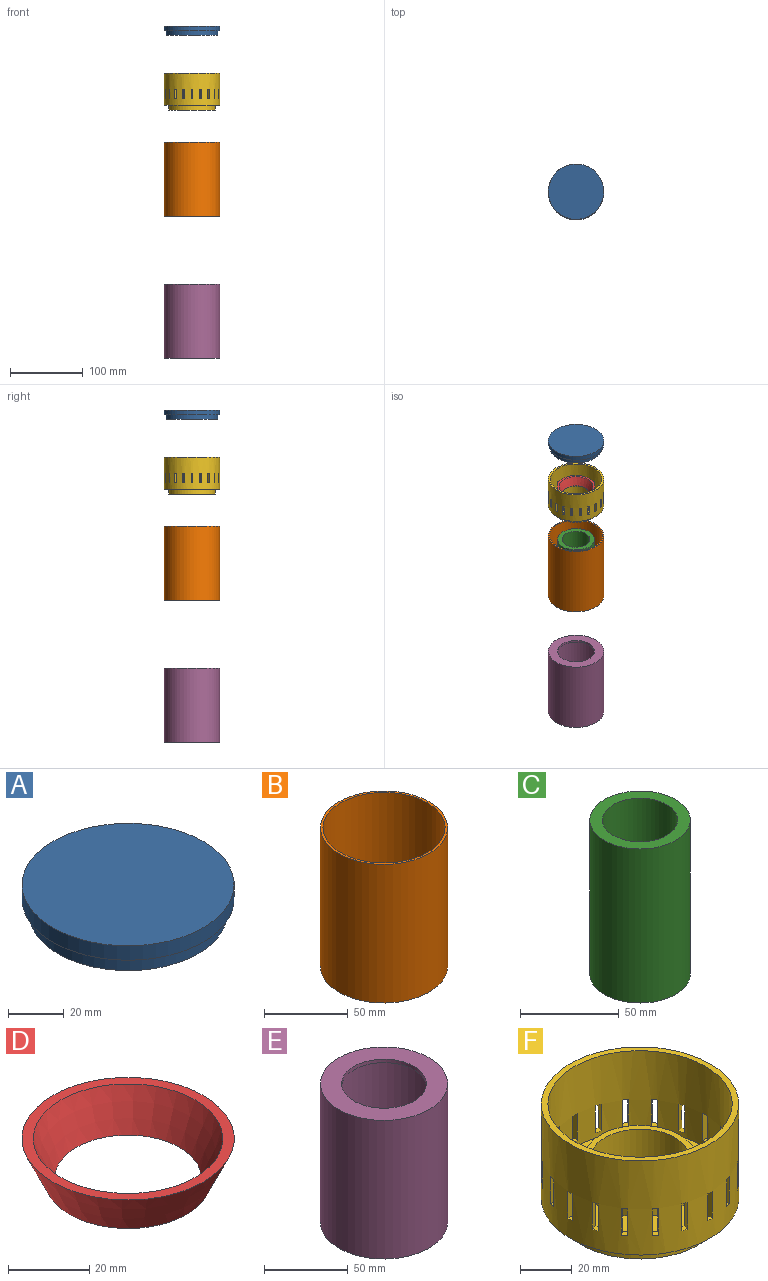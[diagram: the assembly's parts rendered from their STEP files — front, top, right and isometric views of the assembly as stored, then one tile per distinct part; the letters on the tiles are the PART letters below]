
ASSEMBLY  parts=6 mates=2
PART A: 5 faces, bbox 76.2x76.2x12.7 mm
  f0: cylinder r=38.1mm len=76.2mm, axis (0,0,-1), area 1520.1mm2, adj f1,f2
  f1: plane 76.2x76.2mm, normal (0,0,1), area 4560.4mm2, adj f0
  f2: plane 76.2x76.2mm, normal (0,0,-1), area 587.8mm2, adj f0,f3
  f3: cylinder r=35.56mm len=71.12mm, axis (0,0,1), area 1418.8mm2, adj f2,f4
  f4: plane 71.12x71.12mm, normal (0,0,-1), area 3972.6mm2, adj f3
PART B: 4 faces, bbox 76.2x76.2x101.6 mm
  f0: cylinder r=36.58mm len=101.6mm, axis (0,0,-1), area 23349.1mm2, adj f2,f3
  f1: cylinder r=38.1mm len=101.6mm, axis (0,0,-1), area 24322mm2, adj f2,f3
  f2: plane 76.2x76.2mm, normal (0,0,1), area 357.5mm2, adj f0,f1
  f3: plane 76.2x76.2mm, normal (0,0,-1), area 357.5mm2, adj f0,f1
PART C: 4 faces, bbox 50.8x50.8x95.3 mm
  f0: cylinder r=19.05mm len=95.25mm, axis (0,0,-1), area 11400.9mm2, adj f2,f3
  f1: cylinder r=25.4mm len=95.25mm, axis (0,0,-1), area 15201.2mm2, adj f2,f3
  f2: plane 50.8x50.8mm, normal (0,0,1), area 886.7mm2, adj f0,f1
  f3: plane 50.8x50.8mm, normal (0,0,-1), area 886.7mm2, adj f0,f1
PART D: 4 faces, bbox 52.3x52.3x12.7 mm
  f0: cone r=20.32mm half-angle=65.4deg, axis (0,0,-1), area 305.9mm2, adj f1,f2
  f1: cone r=18.01mm half-angle=24.6deg, axis (0,0,1), area 1663.8mm2, adj f0,f3
  f2: cone r=20.32mm half-angle=24.6deg, axis (0,0,1), area 2039mm2, adj f0,f3
  f3: plane 52.28x52.28mm, normal (0,0,1), area 434.4mm2, adj f1,f2
PART E: 6 faces, bbox 76.2x76.2x101.6 mm
  f0: cylinder r=35.56mm len=99.06mm, axis (0,0,-1), area 22133mm2, adj f4,f5
  f1: cylinder r=38.1mm len=101.6mm, axis (0,0,-1), area 24322mm2, adj f2,f5
  f2: plane 76.2x76.2mm, normal (0,0,1), area 2533.5mm2, adj f1,f3
  f3: cylinder r=25.4mm len=50.8mm, axis (0,0,1), area 405.4mm2, adj f2,f4
  f4: plane 71.12x71.12mm, normal (0,0,-1), area 1945.8mm2, adj f0,f3
  f5: plane 76.2x76.2mm, normal (0,0,-1), area 587.8mm2, adj f0,f1
PART F: 90 faces, bbox 76.2x76.2x50.8 mm
  f0: cylinder r=19.05mm len=38.1mm, axis (0,0,-1), area 3040.2mm2, adj f2,f7
  f1: cylinder r=21.59mm len=43.18mm, axis (0,0,-1), area 1722.8mm2, adj f2,f3
  f2: plane 43.18x43.18mm, normal (0,0,1), area 324.3mm2, adj f0,f1
  f3: plane 71.12x71.12mm, normal (0,0,1), area 2508.2mm2, adj f1,f84
  f4: cylinder r=38.1mm len=76.2mm, axis (0,0,1), area 9995.6mm2, adj f5,f8,f9,f10,f11,f12,f13,f14
  f5: plane 76.2x76.2mm, normal (0,0,-1), area 1393.4mm2, adj f4,f6
  f6: cylinder r=31.75mm len=63.5mm, axis (0,0,1), area 1266.8mm2, adj f5,f7
  f7: plane 63.5x63.5mm, normal (0,0,-1), area 2026.8mm2, adj f0,f6
  f8: plane 12.7x2.42mm, normal (0.95,-0.31,0), area 32.3mm2, adj f4,f9,f11,f84
  f9: plane 3.2x3.2mm, normal (0,0,1), area 6.5mm2, adj f4,f8,f10,f84
  f10: plane 12.7x2.42mm, normal (-0.95,0.31,0), area 32.3mm2, adj f4,f9,f11,f84
  f11: plane 3.2x3.2mm, normal (0,0,-1), area 6.5mm2, adj f4,f8,f10,f84
  f12: plane 12.7x2.06mm, normal (0.81,-0.59,0), area 32.3mm2, adj f4,f13,f15,f84
  f13: plane 3.55x3.55mm, normal (0,0,1), area 6.5mm2, adj f4,f12,f14,f84
  f14: plane 12.7x2.06mm, normal (-0.81,0.59,0), area 32.3mm2, adj f4,f13,f15,f84
  f15: plane 3.55x3.55mm, normal (0,0,-1), area 6.5mm2, adj f4,f12,f14,f84
  f16: plane 12.7x2.06mm, normal (0.59,-0.81,0), area 32.3mm2, adj f4,f17,f19,f84
  f17: plane 3.55x3.55mm, normal (0,0,1), area 6.5mm2, adj f4,f16,f18,f84
  f18: plane 12.7x2.06mm, normal (-0.59,0.81,0), area 32.3mm2, adj f4,f17,f19,f84
  f19: plane 3.55x3.55mm, normal (0,0,-1), area 6.5mm2, adj f4,f16,f18,f84
  f20: plane 12.7x2.42mm, normal (0.31,-0.95,0), area 32.3mm2, adj f4,f21,f23,f84
  f21: plane 3.2x3.2mm, normal (0,0,1), area 6.5mm2, adj f4,f20,f22,f84
  f22: plane 12.7x2.42mm, normal (-0.31,0.95,0), area 32.3mm2, adj f4,f21,f23,f84
  f23: plane 3.2x3.2mm, normal (0,0,-1), area 6.5mm2, adj f4,f20,f22,f84
  f24: plane 12.7x2.54mm, normal (0,-1,0), area 32.3mm2, adj f4,f25,f27,f84
  f25: plane 2.56x2.54mm, normal (0,0,1), area 6.5mm2, adj f4,f24,f26,f84
  f26: plane 12.7x2.54mm, normal (0,1,0), area 32.3mm2, adj f4,f25,f27,f84
  f27: plane 2.56x2.54mm, normal (0,0,-1), area 6.5mm2, adj f4,f24,f26,f84
  f28: plane 12.7x2.42mm, normal (-0.31,-0.95,0), area 32.3mm2, adj f4,f29,f31,f84
  f29: plane 3.2x3.2mm, normal (0,0,1), area 6.5mm2, adj f4,f28,f30,f84
  f30: plane 12.7x2.42mm, normal (0.31,0.95,0), area 32.3mm2, adj f4,f29,f31,f84
  f31: plane 3.2x3.2mm, normal (0,0,-1), area 6.5mm2, adj f4,f28,f30,f84
  f32: plane 12.7x2.06mm, normal (-0.59,-0.81,0), area 32.3mm2, adj f4,f33,f35,f84
  f33: plane 3.55x3.55mm, normal (0,0,1), area 6.5mm2, adj f4,f32,f34,f84
  f34: plane 12.7x2.06mm, normal (0.59,0.81,0), area 32.3mm2, adj f4,f33,f35,f84
  f35: plane 3.55x3.55mm, normal (0,0,-1), area 6.5mm2, adj f4,f32,f34,f84
  f36: plane 12.7x2.06mm, normal (-0.81,-0.59,0), area 32.3mm2, adj f4,f37,f39,f84
  f37: plane 3.55x3.55mm, normal (0,0,1), area 6.5mm2, adj f4,f36,f38,f84
  f38: plane 12.7x2.06mm, normal (0.81,0.59,0), area 32.3mm2, adj f4,f37,f39,f84
  f39: plane 3.55x3.55mm, normal (0,0,-1), area 6.5mm2, adj f4,f36,f38,f84
  f40: plane 12.7x2.42mm, normal (-0.95,-0.31,0), area 32.3mm2, adj f4,f41,f43,f84
  f41: plane 3.2x3.2mm, normal (0,0,1), area 6.5mm2, adj f4,f40,f42,f84
  f42: plane 12.7x2.42mm, normal (0.95,0.31,0), area 32.3mm2, adj f4,f41,f43,f84
  f43: plane 3.2x3.2mm, normal (0,0,-1), area 6.5mm2, adj f4,f40,f42,f84
  f44: plane 12.7x2.54mm, normal (-1,0,0), area 32.3mm2, adj f4,f45,f47,f84
  f45: plane 2.56x2.54mm, normal (0,0,1), area 6.5mm2, adj f4,f44,f46,f84
  f46: plane 12.7x2.54mm, normal (1,0,0), area 32.3mm2, adj f4,f45,f47,f84
  f47: plane 2.56x2.54mm, normal (0,0,-1), area 6.5mm2, adj f4,f44,f46,f84
  f48: plane 12.7x2.42mm, normal (-0.95,0.31,0), area 32.3mm2, adj f4,f49,f51,f84
  f49: plane 3.2x3.2mm, normal (0,0,1), area 6.5mm2, adj f4,f48,f50,f84
  f50: plane 12.7x2.42mm, normal (0.95,-0.31,0), area 32.3mm2, adj f4,f49,f51,f84
  f51: plane 3.2x3.2mm, normal (0,0,-1), area 6.5mm2, adj f4,f48,f50,f84
  f52: plane 12.7x2.06mm, normal (-0.81,0.59,0), area 32.3mm2, adj f4,f53,f55,f84
  f53: plane 3.55x3.55mm, normal (0,0,1), area 6.5mm2, adj f4,f52,f54,f84
  f54: plane 12.7x2.06mm, normal (0.81,-0.59,0), area 32.3mm2, adj f4,f53,f55,f84
  f55: plane 3.55x3.55mm, normal (0,0,-1), area 6.5mm2, adj f4,f52,f54,f84
  f56: plane 12.7x2.06mm, normal (-0.59,0.81,0), area 32.3mm2, adj f4,f57,f59,f84
  f57: plane 3.55x3.55mm, normal (0,0,1), area 6.5mm2, adj f4,f56,f58,f84
  f58: plane 12.7x2.06mm, normal (0.59,-0.81,0), area 32.3mm2, adj f4,f57,f59,f84
  f59: plane 3.55x3.55mm, normal (0,0,-1), area 6.5mm2, adj f4,f56,f58,f84
  f60: plane 12.7x2.42mm, normal (-0.31,0.95,0), area 32.3mm2, adj f4,f61,f63,f84
  f61: plane 3.2x3.2mm, normal (0,0,1), area 6.5mm2, adj f4,f60,f62,f84
  f62: plane 12.7x2.42mm, normal (0.31,-0.95,0), area 32.3mm2, adj f4,f61,f63,f84
  f63: plane 3.2x3.2mm, normal (0,0,-1), area 6.5mm2, adj f4,f60,f62,f84
  f64: plane 12.7x2.54mm, normal (0,1,0), area 32.3mm2, adj f4,f65,f67,f84
  f65: plane 2.56x2.54mm, normal (0,0,1), area 6.5mm2, adj f4,f64,f66,f84
  f66: plane 12.7x2.54mm, normal (0,-1,0), area 32.3mm2, adj f4,f65,f67,f84
  f67: plane 2.56x2.54mm, normal (0,0,-1), area 6.5mm2, adj f4,f64,f66,f84
  f68: plane 12.7x2.42mm, normal (0.31,0.95,0), area 32.3mm2, adj f4,f69,f71,f84
  f69: plane 3.2x3.2mm, normal (0,0,1), area 6.5mm2, adj f4,f68,f70,f84
  f70: plane 12.7x2.42mm, normal (-0.31,-0.95,0), area 32.3mm2, adj f4,f69,f71,f84
  f71: plane 3.2x3.2mm, normal (0,0,-1), area 6.5mm2, adj f4,f68,f70,f84
  f72: plane 12.7x2.06mm, normal (0.59,0.81,0), area 32.3mm2, adj f4,f73,f75,f84
  f73: plane 3.55x3.55mm, normal (0,0,1), area 6.5mm2, adj f4,f72,f74,f84
  f74: plane 12.7x2.06mm, normal (-0.59,-0.81,0), area 32.3mm2, adj f4,f73,f75,f84
  f75: plane 3.55x3.55mm, normal (0,0,-1), area 6.5mm2, adj f4,f72,f74,f84
  f76: plane 12.7x2.06mm, normal (0.81,0.59,0), area 32.3mm2, adj f4,f77,f79,f84
  f77: plane 3.55x3.55mm, normal (0,0,1), area 6.5mm2, adj f4,f76,f78,f84
  f78: plane 12.7x2.06mm, normal (-0.81,-0.59,0), area 32.3mm2, adj f4,f77,f79,f84
  f79: plane 3.55x3.55mm, normal (0,0,-1), area 6.5mm2, adj f4,f76,f78,f84
  f80: plane 12.7x2.42mm, normal (0.95,0.31,0), area 32.3mm2, adj f4,f81,f83,f84
  f81: plane 3.2x3.2mm, normal (0,0,1), area 6.5mm2, adj f4,f80,f82,f84
  f82: plane 12.7x2.42mm, normal (-0.95,-0.31,0), area 32.3mm2, adj f4,f81,f83,f84
  f83: plane 3.2x3.2mm, normal (0,0,-1), area 6.5mm2, adj f4,f80,f82,f84
  f84: cylinder r=35.56mm len=71.12mm, axis (0,0,-1), area 7867.4mm2, adj f3,f8,f9,f10,f11,f12,f13,f14
  f85: plane 76.2x76.2mm, normal (0,0,1), area 587.8mm2, adj f4,f84
  f86: plane 12.7x2.54mm, normal (1,0,0), area 32.3mm2, adj f4,f84,f87,f89
  f87: plane 2.56x2.54mm, normal (0,0,1), area 6.5mm2, adj f4,f84,f86,f88
  f88: plane 12.7x2.54mm, normal (-1,0,0), area 32.3mm2, adj f4,f84,f87,f89
  f89: plane 2.56x2.54mm, normal (0,0,-1), area 6.5mm2, adj f4,f84,f86,f88
PLACE A t=(0,0,306.07)mm
PLACE B t=(0,0,50.8)mm
PLACE C t=(0,0,50.8)mm
PLACE D t=(0,0,209.55)mm
PLACE E t=(0,0,-67.82)mm
PLACE F t=(0,0,209.55)mm
MATE slider F.f4 <-> B.f1  axis (0,0,-1) through (0,0,203.2)mm
MATE fastened D.f0 <-> F.f1  axis (0,0,1) through (0,0,222.25)mm
